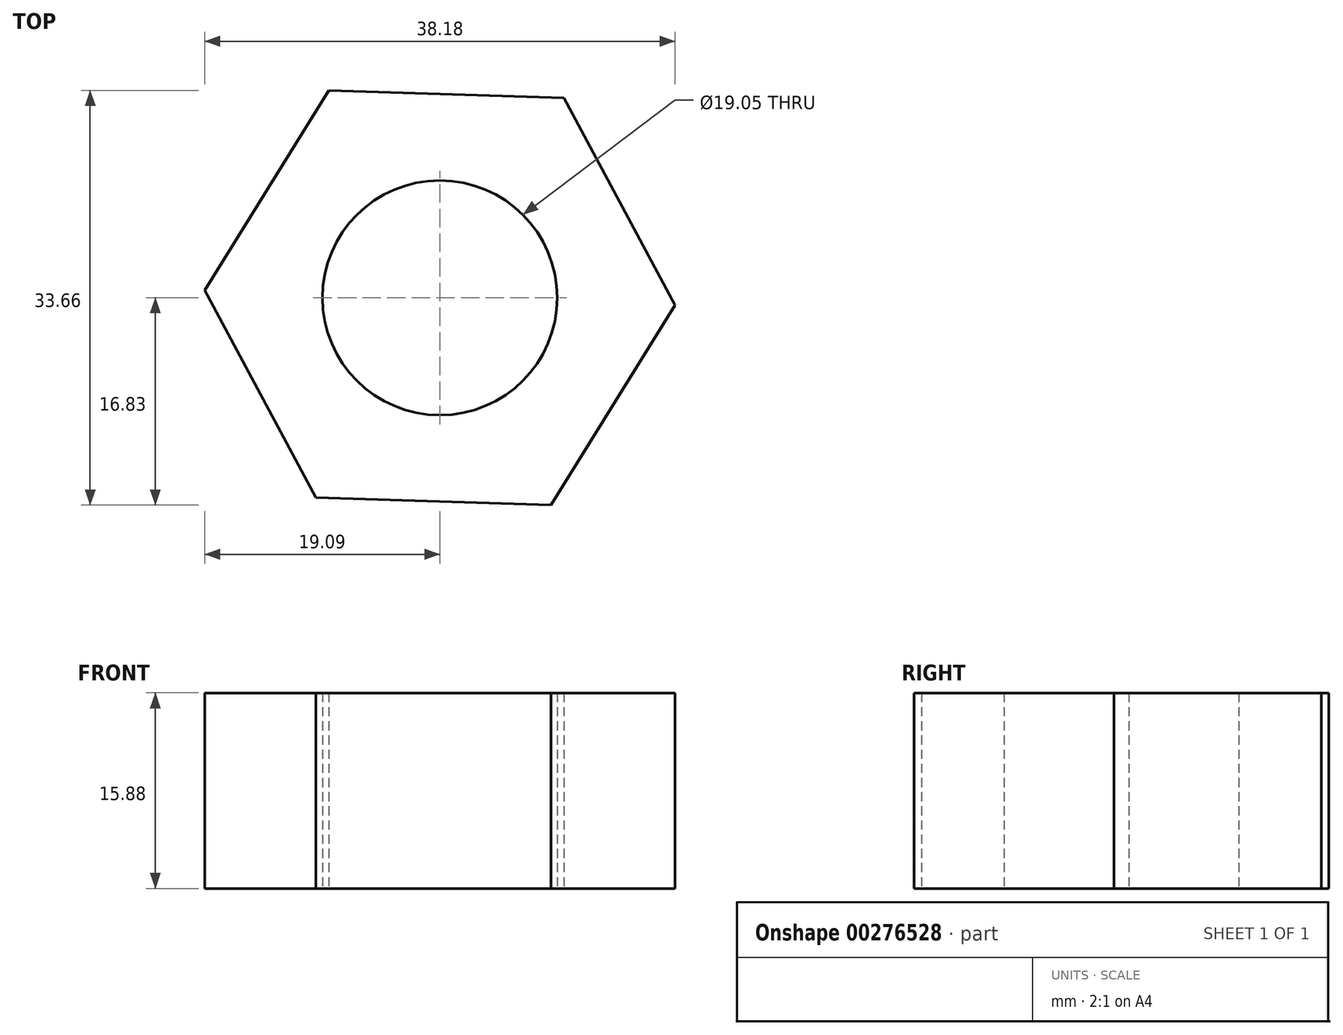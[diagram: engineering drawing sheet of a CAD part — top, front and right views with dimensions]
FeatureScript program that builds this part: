
annotation { "Feature Type Name" : "Feature", "Feature Type Description" : "" }
export const myFeature = defineFeature(function(context is Context, id is Id, definition is map)
    precondition{}
    {
        {
            var Q0;
            Q0=qCreatedBy(makeId("Top.planeOp"),FACE);
            var sketch = newSketch(context, id + "F0", { "sketchPlane" : qUnion([Q0])});
            skCircle(sketch, "E0", {"center": v(0, 0) * mm, "radius": 9.53 * mm});
            skCircle(sketch, "E1.cCircle", {"center": v(0, 0) * mm, "radius": 16.54 * mm});
            skLineSegment(sketch, "E1.0", {"start": v(19.09, -0.6) * mm, "end": v(9.03, -16.83) * mm});
            skLineSegment(sketch, "E1.1", {"start": v(9.03, -16.83) * mm, "end": v(-10.06, -16.23) * mm});
            skLineSegment(sketch, "E1.2", {"start": v(-10.06, -16.23) * mm, "end": v(-19.09, 0.6) * mm});
            skLineSegment(sketch, "E1.3", {"start": v(-19.09, 0.6) * mm, "end": v(-9.03, 16.83) * mm});
            skLineSegment(sketch, "E1.4", {"start": v(-9.03, 16.83) * mm, "end": v(10.06, 16.23) * mm});
            skLineSegment(sketch, "E1.5", {"start": v(10.06, 16.23) * mm, "end": v(19.09, -0.6) * mm});
            skPoint(sketch, "E1.0.midPoint", {"position": v(14.06, -8.71) * mm});
            skSolve(sketch);
        }
        {
            var Q0;
            Q0 = qSketchRegion(id + "F0", true);
            extrude(context, id + "F1", {"entities" : qUnion([Q0]), "depth" : 15.88 * mm});
        }
    });
